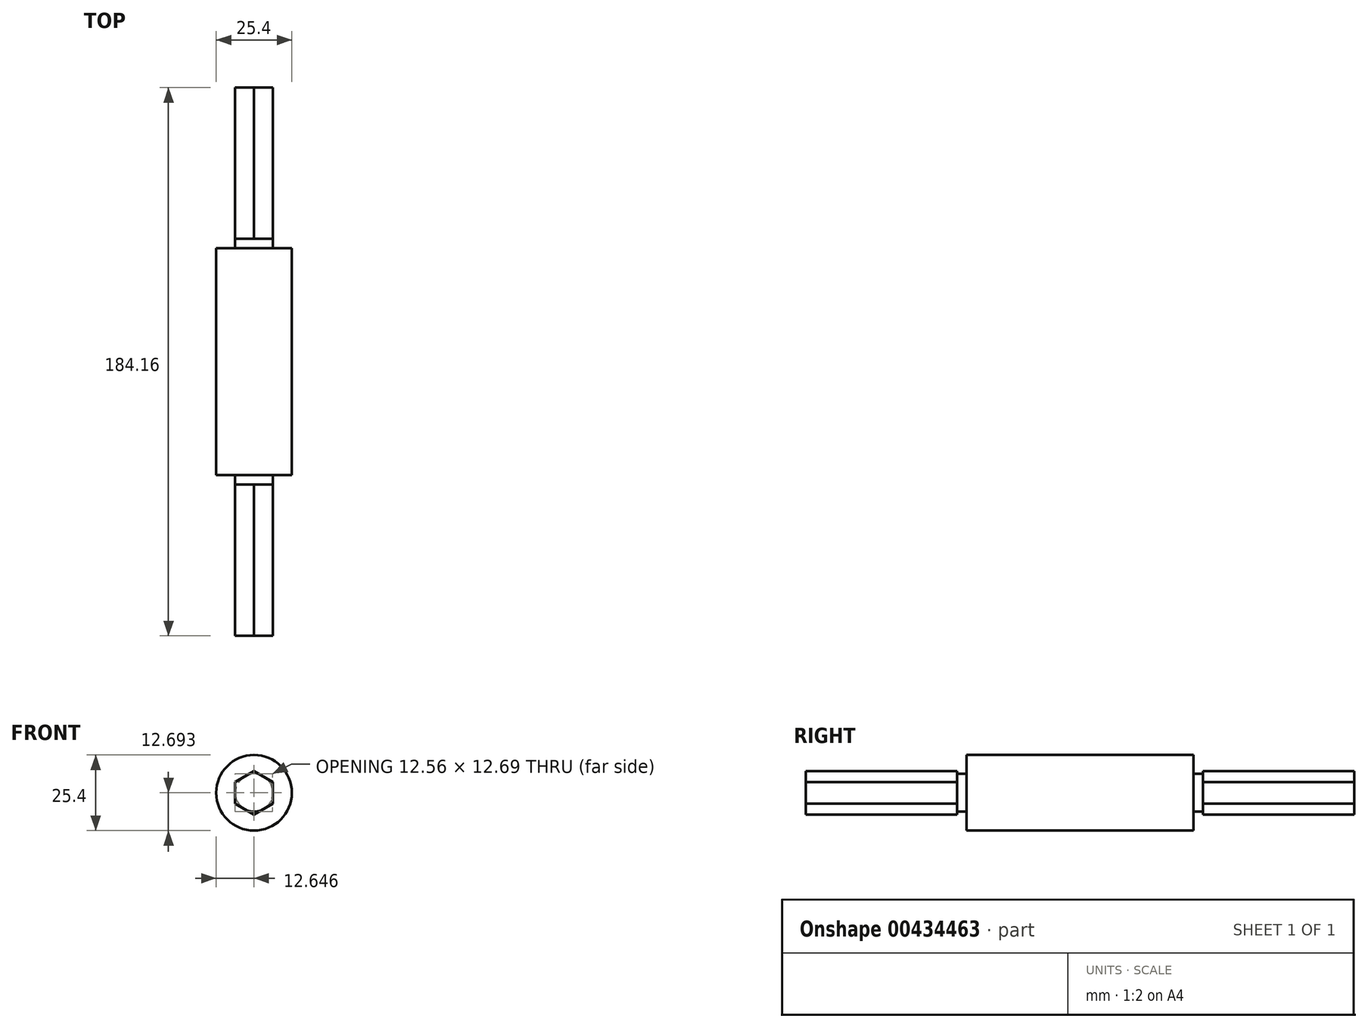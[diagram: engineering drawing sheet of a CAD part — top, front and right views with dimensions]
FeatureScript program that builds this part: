
annotation { "Feature Type Name" : "Feature", "Feature Type Description" : "" }
export const myFeature = defineFeature(function(context is Context, id is Id, definition is map)
    precondition{}
    {
        {
            var Q0;
            Q0=qCreatedBy(makeId("Front.planeOp"),FACE);
            var sketch = newSketch(context, id + "F0", { "sketchPlane" : qUnion([Q0])});
            skCircle(sketch, "E0", {"center": v(0, 0) * mm, "radius": 12.7 * mm});
            skCircle(sketch, "E1.cCircle", {"center": v(0, 0) * mm, "radius": 6.35 * mm});
            skLineSegment(sketch, "E1.0", {"start": v(-3.67, 6.35) * mm, "end": v(3.67, 6.35) * mm});
            skLineSegment(sketch, "E1.1", {"start": v(3.67, 6.35) * mm, "end": v(7.33, 0) * mm});
            skLineSegment(sketch, "E1.2", {"start": v(7.33, 0) * mm, "end": v(3.67, -6.35) * mm});
            skLineSegment(sketch, "E1.3", {"start": v(3.67, -6.35) * mm, "end": v(-3.67, -6.35) * mm});
            skLineSegment(sketch, "E1.4", {"start": v(-3.67, -6.35) * mm, "end": v(-7.33, 0) * mm});
            skLineSegment(sketch, "E1.5", {"start": v(-7.33, 0) * mm, "end": v(-3.67, 6.35) * mm});
            skPoint(sketch, "E1.0.midPoint", {"position": v(0, 6.35) * mm});
            skSolve(sketch);
        }
        {
            var Q0;
            {var subQ0=sQuery(id+"F0.wireOp",EDGE,"E1.0");var subQ1=sQuery(id+"F0.wireOp",EDGE,"E1.cCircle");var subQ2=makeQuery(id+"F0.imprint","INTERSECT",VERTEX,{"derivedFrom":[subQ1,subQ0]});Q0=makeQuery(id+"F0.imprint","IMPRINT",FACE,{"disambiguationData":[TD([[makeQuery(id+"F0.imprint","IMPRINT",EDGE,{"disambiguationData":[TD([[subQ2,1.0]])],"derivedFrom":subQ1}),-1.0]])]});}
            var Q1;
            {var subQ0=sQuery(id+"F0.wireOp",EDGE,"E1.1");var subQ1=sQuery(id+"F0.wireOp",EDGE,"E1.cCircle");var subQ2=makeQuery(id+"F0.imprint","INTERSECT",VERTEX,{"derivedFrom":[subQ1,subQ0]});Q1=makeQuery(id+"F0.imprint","IMPRINT",FACE,{"disambiguationData":[TD([[makeQuery(id+"F0.imprint","IMPRINT",EDGE,{"disambiguationData":[TD([[subQ2,1.0]])],"derivedFrom":subQ1}),-1.0]])]});}
            var Q2;
            {var subQ0=sQuery(id+"F0.wireOp",EDGE,"E1.0");var subQ1=sQuery(id+"F0.wireOp",EDGE,"E1.cCircle");var subQ2=makeQuery(id+"F0.imprint","INTERSECT",VERTEX,{"derivedFrom":[subQ1,subQ0]});Q2=makeQuery(id+"F0.imprint","IMPRINT",FACE,{"disambiguationData":[TD([[makeQuery(id+"F0.imprint","IMPRINT",EDGE,{"disambiguationData":[TD([[subQ2,-1.0]])],"derivedFrom":subQ1}),-1.0]])]});}
            var Q3;
            Q3=makeQuery(id+"F0.imprint","IMPRINT",FACE,{"disambiguationData":[TD([[makeQuery(id+"F0.imprint","IMPRINT",EDGE,{"derivedFrom":sQuery(id+"F0.wireOp",EDGE,"E0")}),1.0]])]});
            var Q4;
            {var subQ0=sQuery(id+"F0.wireOp",EDGE,"E1.5");var subQ1=sQuery(id+"F0.wireOp",EDGE,"E1.cCircle");var subQ2=makeQuery(id+"F0.imprint","INTERSECT",VERTEX,{"derivedFrom":[subQ1,subQ0]});Q4=makeQuery(id+"F0.imprint","IMPRINT",FACE,{"disambiguationData":[TD([[makeQuery(id+"F0.imprint","IMPRINT",EDGE,{"disambiguationData":[TD([[subQ2,-1.0]])],"derivedFrom":subQ1}),-1.0]])]});}
            var Q5;
            {var subQ0=sQuery(id+"F0.wireOp",EDGE,"E1.4");var subQ1=sQuery(id+"F0.wireOp",EDGE,"E1.cCircle");var subQ2=makeQuery(id+"F0.imprint","INTERSECT",VERTEX,{"derivedFrom":[subQ1,subQ0]});Q5=makeQuery(id+"F0.imprint","IMPRINT",FACE,{"disambiguationData":[TD([[makeQuery(id+"F0.imprint","IMPRINT",EDGE,{"disambiguationData":[TD([[subQ2,-1.0]])],"derivedFrom":subQ1}),-1.0]])]});}
            var Q6;
            {var subQ0=sQuery(id+"F0.wireOp",EDGE,"E1.3");var subQ1=sQuery(id+"F0.wireOp",EDGE,"E1.cCircle");var subQ2=makeQuery(id+"F0.imprint","INTERSECT",VERTEX,{"derivedFrom":[subQ1,subQ0]});Q6=makeQuery(id+"F0.imprint","IMPRINT",FACE,{"disambiguationData":[TD([[makeQuery(id+"F0.imprint","IMPRINT",EDGE,{"disambiguationData":[TD([[subQ2,-1.0]])],"derivedFrom":subQ1}),-1.0]])]});}
            extrude(context, id + "F1", {"entities" : qUnion([Q0, Q1, Q2, Q3, Q4, Q5, Q6]), "depth" : 76.2 * mm});
        }
        {
            var Q0;
            {var subQ0=sQuery(id+"F0.wireOp",EDGE,"E1.cCircle");var subQ4=makeQuery(id+"F0.imprint","INTERSECT",VERTEX,{"derivedFrom":[subQ0,sQuery(id+"F0.wireOp",EDGE,"E1.0")]});Q0=makeQuery(id+"F0.imprint","IMPRINT",FACE,{"disambiguationData":[TD([[makeQuery(id+"F0.imprint","IMPRINT",EDGE,{"disambiguationData":[TD([[subQ4,1.0]])],"derivedFrom":subQ0}),1.0]])]});}
            extrude(context, id + "F2", {"entities" : qUnion([Q0]), "operationType" : NewBodyOperationType.ADD, "depth" : 79.38 * mm, "hasSecondDirection" : true, "secondDirectionOppositeDirection" : true, "secondDirectionDepth" : 3.17 * mm});
        }
        {
            var Q0;
            Q0=makeQuery(id+"F2.opExtrude","CAP_FACE",FACE,{"disambiguationData":[OSD([sQuery(id+"F0.wireOp",EDGE,"E1.cCircle")])],"isStart":true});
            var sketch = newSketch(context, id + "F3", { "sketchPlane" : qUnion([Q0])});
            skCircle(sketch, "E2.cCircle", {"center": v(0, 0) * mm, "radius": 6.35 * mm, "construction": true});
            skLineSegment(sketch, "E2.0", {"start": v(6.35, 3.67) * mm, "end": v(6.35, -3.67) * mm});
            skLineSegment(sketch, "E2.1", {"start": v(6.35, -3.67) * mm, "end": v(0, -7.33) * mm});
            skLineSegment(sketch, "E2.2", {"start": v(0, -7.33) * mm, "end": v(-6.35, -3.67) * mm});
            skLineSegment(sketch, "E2.3", {"start": v(-6.35, -3.67) * mm, "end": v(-6.35, 3.67) * mm});
            skLineSegment(sketch, "E2.4", {"start": v(-6.35, 3.67) * mm, "end": v(0, 7.33) * mm});
            skLineSegment(sketch, "E2.5", {"start": v(0, 7.33) * mm, "end": v(6.35, 3.67) * mm});
            skPoint(sketch, "E2.0.midPoint", {"position": v(6.35, 0) * mm});
            skSolve(sketch);
        }
        {
            var Q0;
            Q0 = qSketchRegion(id + "F3", true);
            extrude(context, id + "F4", {"entities" : qUnion([Q0]), "operationType" : NewBodyOperationType.ADD, "depth" : 50.8 * mm});
        }
        {
            var Q0;
            Q0=makeQuery(id+"F2.opExtrude","CAP_FACE",FACE,{"disambiguationData":[OSD([sQuery(id+"F0.wireOp",EDGE,"E1.cCircle")])],"isStart":false});
            var sketch = newSketch(context, id + "F5", { "sketchPlane" : qUnion([Q0])});
            skCircle(sketch, "E3.cCircle", {"center": v(0, 0) * mm, "radius": 6.35 * mm, "construction": true});
            skLineSegment(sketch, "E3.0", {"start": v(-6.35, -3.67) * mm, "end": v(-6.35, 3.67) * mm});
            skLineSegment(sketch, "E3.1", {"start": v(-6.35, 3.67) * mm, "end": v(0, 7.33) * mm});
            skLineSegment(sketch, "E3.2", {"start": v(0, 7.33) * mm, "end": v(6.35, 3.67) * mm});
            skLineSegment(sketch, "E3.3", {"start": v(6.35, 3.67) * mm, "end": v(6.35, -3.67) * mm});
            skLineSegment(sketch, "E3.4", {"start": v(6.35, -3.67) * mm, "end": v(0, -7.33) * mm});
            skLineSegment(sketch, "E3.5", {"start": v(0, -7.33) * mm, "end": v(-6.35, -3.67) * mm});
            skPoint(sketch, "E3.0.midPoint", {"position": v(-6.35, 0) * mm});
            skSolve(sketch);
        }
        {
            var Q0;
            Q0 = qSketchRegion(id + "F5", true);
            extrude(context, id + "F6", {"entities" : qUnion([Q0]), "operationType" : NewBodyOperationType.ADD, "depth" : 50.8 * mm});
        }
    });
